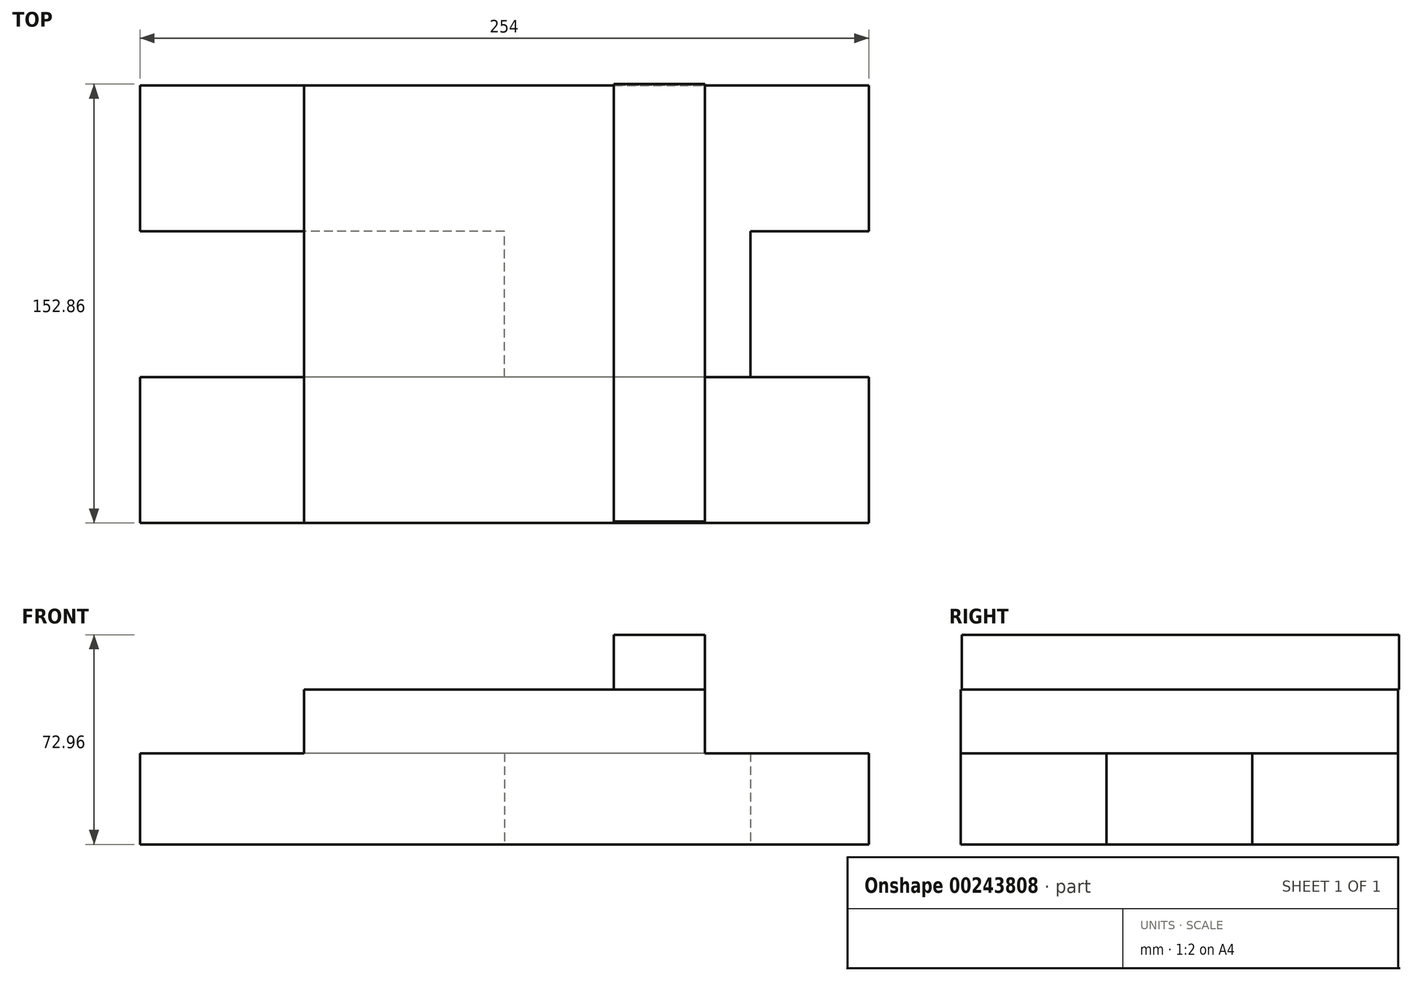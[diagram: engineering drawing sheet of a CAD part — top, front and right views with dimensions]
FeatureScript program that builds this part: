
annotation { "Feature Type Name" : "Feature", "Feature Type Description" : "" }
export const myFeature = defineFeature(function(context is Context, id is Id, definition is map)
    precondition{}
    {
        {
            var Q0;
            Q0=qCreatedBy(makeId("Right.planeOp"),FACE);
            var sketch = newSketch(context, id + "F0", { "sketchPlane" : qUnion([Q0])});
            skLineSegment(sketch, "E0.bottom", {"start": v(-89.36, 0) * mm, "end": v(-38.56, 0) * mm});
            skLineSegment(sketch, "E0.top", {"start": v(-89.36, -31.75) * mm, "end": v(-38.56, -31.75) * mm});
            skLineSegment(sketch, "E0.left", {"start": v(-89.36, 0) * mm, "end": v(-89.36, -31.75) * mm});
            skLineSegment(sketch, "E0.right", {"start": v(-38.56, 0) * mm, "end": v(-38.56, -31.75) * mm});
            skLineSegment(sketch, "E1.bottom", {"start": v(-38.53, 0) * mm, "end": v(12.27, 0) * mm});
            skLineSegment(sketch, "E1.top", {"start": v(-38.53, -31.75) * mm, "end": v(12.27, -31.75) * mm});
            skLineSegment(sketch, "E1.left", {"start": v(-38.53, 0) * mm, "end": v(-38.53, -31.75) * mm});
            skLineSegment(sketch, "E1.right", {"start": v(12.27, 0) * mm, "end": v(12.27, -31.75) * mm});
            skLineSegment(sketch, "E2.bottom", {"start": v(12.27, 0) * mm, "end": v(63.07, 0) * mm});
            skLineSegment(sketch, "E2.top", {"start": v(12.27, -31.75) * mm, "end": v(63.07, -31.75) * mm});
            skLineSegment(sketch, "E2.right", {"start": v(63.07, 0) * mm, "end": v(63.07, -31.75) * mm});
            skLineSegment(sketch, "E3.bottom", {"start": v(-89.36, 0) * mm, "end": v(63.04, 0) * mm});
            skLineSegment(sketch, "E3.top", {"start": v(-89.36, 22.23) * mm, "end": v(63.04, 22.23) * mm});
            skLineSegment(sketch, "E3.left", {"start": v(-89.36, 0) * mm, "end": v(-89.36, 22.23) * mm});
            skLineSegment(sketch, "E3.right", {"start": v(63.04, 0) * mm, "end": v(63.04, 22.23) * mm});
            skLineSegment(sketch, "E4.bottom", {"start": v(-89.36, 22.23) * mm, "end": v(-57.6, 22.23) * mm});
            skLineSegment(sketch, "E4.top", {"start": v(-89.36, 53.98) * mm, "end": v(-57.6, 53.98) * mm});
            skLineSegment(sketch, "E4.left", {"start": v(-89.36, 22.23) * mm, "end": v(-89.36, 53.98) * mm});
            skLineSegment(sketch, "E4.right", {"start": v(-57.6, 22.23) * mm, "end": v(-57.6, 53.98) * mm});
            skLineSegment(sketch, "E5.bottom", {"start": v(63.04, 22.23) * mm, "end": v(31.3, 22.23) * mm});
            skLineSegment(sketch, "E5.top", {"start": v(63.04, 53.98) * mm, "end": v(31.3, 53.98) * mm});
            skLineSegment(sketch, "E5.left", {"start": v(63.04, 22.23) * mm, "end": v(63.04, 53.98) * mm});
            skLineSegment(sketch, "E5.right", {"start": v(31.3, 22.23) * mm, "end": v(31.3, 53.97) * mm});
            skSolve(sketch);
        }
        {
            var Q0;
            Q0=makeQuery(id+"F0.imprint","IMPRINT",FACE,{"disambiguationData":[TD([[makeQuery(id+"F0.imprint","IMPRINT",EDGE,{"derivedFrom":sQuery(id+"F0.wireOp",EDGE,"E3.top")}),-1.0]])]});
            extrude(context, id + "F1", {"entities" : qUnion([Q0]), "depth" : 69.85 * mm, "hasSecondDirection" : true, "secondDirectionOppositeDirection" : true, "secondDirectionDepth" : 69.85 * mm});
        }
        {
            var Q0;
            Q0=makeQuery(id+"F0.imprint","IMPRINT",FACE,{"disambiguationData":[TD([[makeQuery(id+"F0.imprint","IMPRINT",EDGE,{"derivedFrom":sQuery(id+"F0.wireOp",EDGE,"E1.top")}),1.0]])]});
            extrude(context, id + "F2", {"entities" : qUnion([Q0]), "operationType" : NewBodyOperationType.ADD, "depth" : 85.72 * mm});
        }
        {
            var Q0;
            Q0=makeQuery(id+"F0.imprint","IMPRINT",FACE,{"disambiguationData":[TD([[makeQuery(id+"F0.imprint","IMPRINT",EDGE,{"derivedFrom":sQuery(id+"F0.wireOp",EDGE,"E0.top")}),1.0]])]});
            var Q1;
            {var subQ1=sQuery(id+"F0.wireOp",EDGE,"E2.bottom");Q1=makeQuery(id+"F0.imprint","IMPRINT",FACE,{"disambiguationData":[TD([[makeQuery(id+"F0.imprint","IMPRINT",EDGE,{"derivedFrom":subQ1}),-1.0]])]});}
            extrude(context, id + "F3", {"entities" : qUnion([Q0, Q1]), "operationType" : NewBodyOperationType.ADD, "depth" : 127 * mm, "hasSecondDirection" : true, "secondDirectionOppositeDirection" : true, "secondDirectionDepth" : 127 * mm});
        }
        {
            var Q0;
            Q0=qCreatedBy(makeId("Front.planeOp"),FACE);
            var sketch = newSketch(context, id + "F4", { "sketchPlane" : qUnion([Q0])});
            skLineSegment(sketch, "E6.bottom", {"start": v(69.86, 41.2) * mm, "end": v(38.1, 41.2) * mm});
            skLineSegment(sketch, "E6.top", {"start": v(69.86, 22.16) * mm, "end": v(38.1, 22.16) * mm});
            skLineSegment(sketch, "E6.left", {"start": v(69.86, 41.2) * mm, "end": v(69.86, 22.16) * mm});
            skLineSegment(sketch, "E6.right", {"start": v(38.1, 41.2) * mm, "end": v(38.1, 22.16) * mm});
            skLineSegment(sketch, "E7.bottom", {"start": v(38.1, 41.2) * mm, "end": v(69.86, 41.2) * mm});
            skLineSegment(sketch, "E7.top", {"start": v(38.1, 60.26) * mm, "end": v(69.86, 60.26) * mm});
            skLineSegment(sketch, "E7.left", {"start": v(38.1, 41.2) * mm, "end": v(38.1, 60.26) * mm});
            skLineSegment(sketch, "E7.right", {"start": v(69.86, 41.2) * mm, "end": v(69.86, 60.26) * mm});
            skSolve(sketch);
        }
        {
            var Q0;
            Q0=makeQuery(id+"F4.imprint","IMPRINT",FACE,{"disambiguationData":[TD([[makeQuery(id+"F4.imprint","IMPRINT",EDGE,{"derivedFrom":sQuery(id+"F4.wireOp",EDGE,"E6.top")}),-1.0]])]});
            extrude(context, id + "F5", {"entities" : qUnion([Q0]), "operationType" : NewBodyOperationType.ADD, "depth" : 88.9 * mm, "hasSecondDirection" : true, "secondDirectionOppositeDirection" : true, "secondDirectionDepth" : 63.5 * mm});
        }
    });
